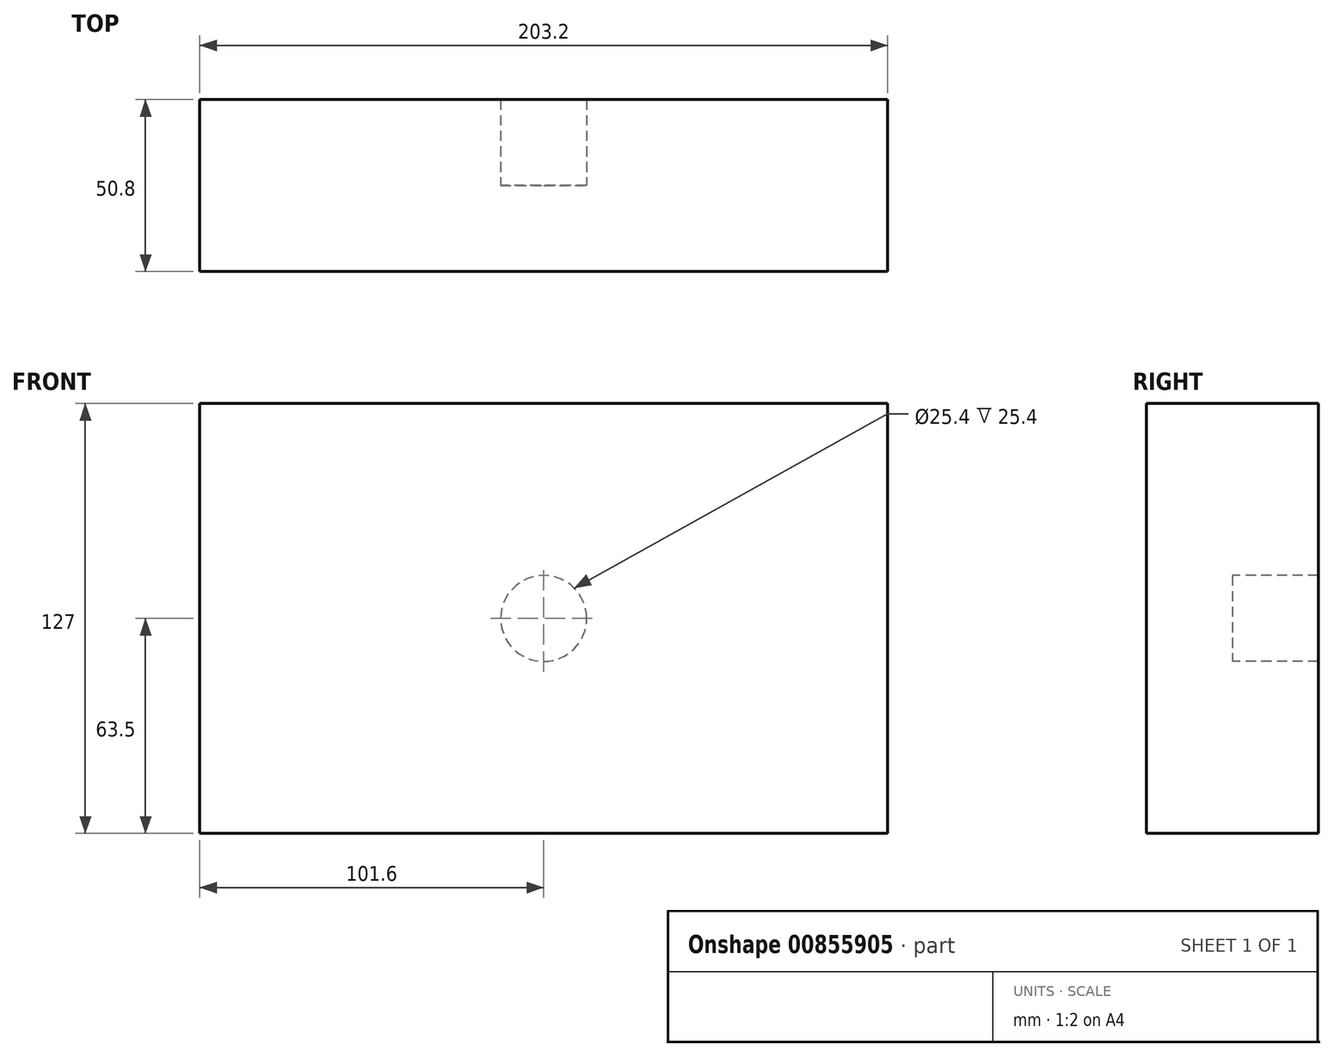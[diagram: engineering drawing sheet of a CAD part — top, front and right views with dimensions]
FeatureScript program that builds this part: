
annotation { "Feature Type Name" : "Feature", "Feature Type Description" : "" }
export const myFeature = defineFeature(function(context is Context, id is Id, definition is map)
    precondition{}
    {
        {
            var Q0;
            Q0=qCreatedBy(makeId("Front.planeOp"),FACE);
            var sketch = newSketch(context, id + "F0", { "sketchPlane" : qUnion([Q0])});
            skLineSegment(sketch, "E0.bottom", {"start": v(101.6, -63.5) * mm, "end": v(-101.6, -63.5) * mm});
            skLineSegment(sketch, "E0.top", {"start": v(101.6, 63.5) * mm, "end": v(-101.6, 63.5) * mm});
            skLineSegment(sketch, "E0.left", {"start": v(101.6, -63.5) * mm, "end": v(101.6, 63.5) * mm});
            skLineSegment(sketch, "E0.right", {"start": v(-101.6, -63.5) * mm, "end": v(-101.6, 63.5) * mm});
            skPoint(sketch, "E0.middle", {"position": v(0, 0) * mm});
            skSolve(sketch);
        }
        {
            var Q0;
            Q0 = qSketchRegion(id + "F0", true);
            extrude(context, id + "F1", {"entities" : qUnion([Q0]), "depth" : 25.4 * mm, "offsetDistance" : 25.4 * mm});
        }
        {
            var Q0;
            Q0=makeQuery(id+"F1.opExtrude","CAP_FACE",FACE,{"disambiguationData":[OSD([sQuery(id+"F0.wireOp",EDGE,"E0.bottom"),sQuery(id+"F0.wireOp",EDGE,"E0.top"),sQuery(id+"F0.wireOp",EDGE,"E0.left"),sQuery(id+"F0.wireOp",EDGE,"E0.right")])],"isStart":true});
            var sketch = newSketch(context, id + "F2", { "sketchPlane" : qUnion([Q0])});
            skCircle(sketch, "E1", {"center": v(0, 0) * mm, "radius": 12.7 * mm});
            skSolve(sketch);
        }
        {
            var Q0;
            Q0=makeQuery(id+"F2.imprint","IMPRINT",FACE,{"disambiguationData":[TD([[makeQuery(id+"F2.imprint","IMPRINT",EDGE,{"derivedFrom":sQuery(id+"F2.wireOp",EDGE,"E1")}),-1.0]])]});
            extrude(context, id + "F3", {"entities" : qUnion([Q0]), "operationType" : NewBodyOperationType.ADD, "depth" : 25.4 * mm, "offsetDistance" : 25.4 * mm});
        }
    });
